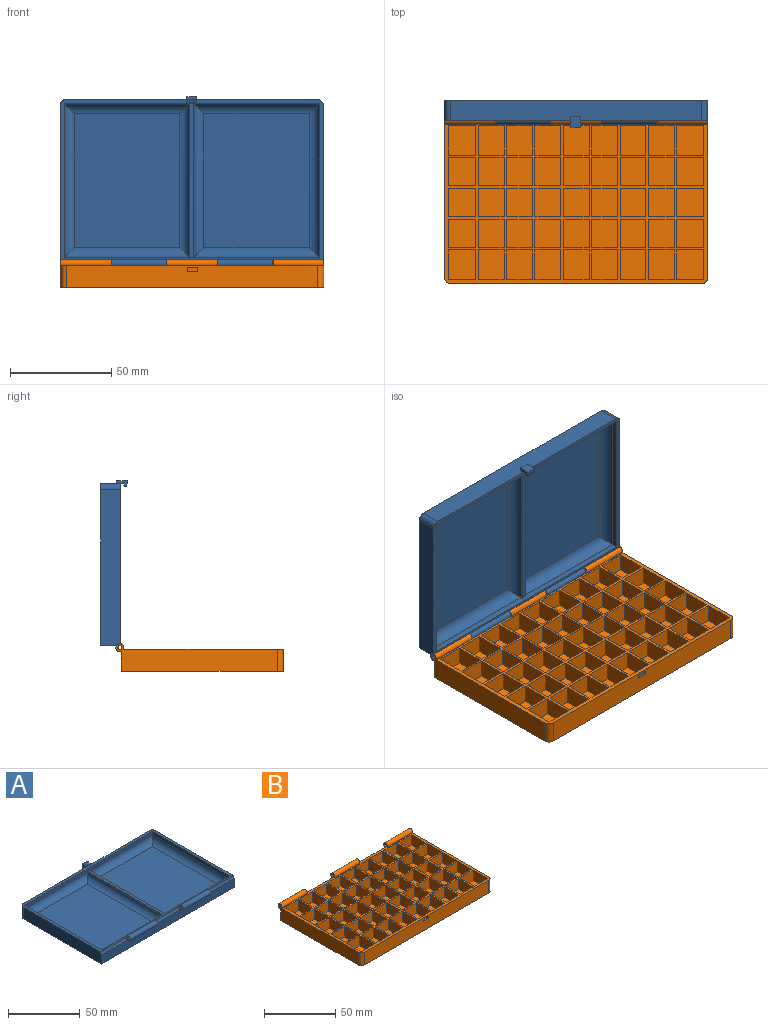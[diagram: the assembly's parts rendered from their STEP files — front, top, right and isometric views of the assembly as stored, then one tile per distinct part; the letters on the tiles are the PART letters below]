
ASSEMBLY  parts=2 mates=1
PART A: 45 faces, bbox 130x84.5x13.2 mm
  f0: cylinder r=2mm len=25mm, axis (1,0,0), area 62.8mm2, adj f2,f9,f20,f24
  f1: cylinder r=2mm len=25.25mm, axis (1,0,0), area 63.5mm2, adj f2,f3,f9,f21
  f2: plane 130x79.06mm, normal (0,0,1), area 697.5mm2, adj f0,f1,f3,f4,f5,f7,f8,f11
  f3: plane 77x10mm, normal (1,0,0), area 768.4mm2, adj f1,f2,f9,f10,f43
  f4: plane 126x3mm, normal (0,-1,0), area 376mm2, adj f2,f11,f12,f14,f15,f16,f36,f40
  f5: plane 126x3mm, normal (0,1,0), area 376mm2, adj f2,f11,f12,f14,f15,f16,f37,f41
  f6: plane 66x52mm, normal (0,0,1), area 3432mm2, adj f35,f36,f37,f38
  f7: plane 124x10mm, normal (0,1,0), area 1230.4mm2, adj f2,f10,f31,f33,f34,f43,f44
  f8: plane 77x10mm, normal (-1,0,0), area 768.4mm2, adj f2,f9,f10,f17,f44
  f9: plane 130x7.85mm, normal (0,-1,0), area 1020mm2, adj f0,f1,f3,f8,f10,f17,f18,f22
  f10: plane 130x80mm, normal (0,0,-1), area 10396.1mm2, adj f3,f7,f8,f9,f43,f44
  f11: plane 76x3mm, normal (1,0,0), area 228mm2, adj f2,f4,f5,f39
  f12: plane 76x3mm, normal (-1,0,0), area 228mm2, adj f2,f4,f5,f35
  f13: plane 66x52mm, normal (0,0,1), area 3432mm2, adj f39,f40,f41,f42
  f14: plane 76x2mm, normal (0,0,1), area 152mm2, adj f4,f5,f15,f16
  f15: plane 76x1mm, normal (1,0,0), area 76mm2, adj f4,f5,f14,f38
  f16: plane 76x1mm, normal (-1,0,0), area 76mm2, adj f4,f5,f14,f42
  f17: cylinder r=2mm len=25.25mm, axis (1,0,0), area 63.5mm2, adj f2,f8,f9,f25
  f18: cylinder r=2mm len=27.25mm, axis (1,0,0), area 273.9mm2, adj f2,f9,f20,f21
  f19: cylinder r=1mm len=27.25mm, axis (1,0,0), area 171.2mm2, adj f20,f21
  f20: plane 4x4mm, normal (-1,0,0), area 9.4mm2, adj f0,f18,f19
  f21: plane 4x4mm, normal (1,0,0), area 9.4mm2, adj f1,f18,f19
  f22: cylinder r=2mm len=27.25mm, axis (-1,0,0), area 273.9mm2, adj f2,f9,f24,f25
  f23: cylinder r=1mm len=27.25mm, axis (-1,0,0), area 171.2mm2, adj f24,f25
  f24: plane 4x4mm, normal (1,0,0), area 9.4mm2, adj f0,f22,f23
  f25: plane 4x4mm, normal (-1,0,0), area 9.4mm2, adj f17,f22,f23
  f26: plane 4.8x1.4mm, normal (0,-0.34,-0.94), area 7.1mm2, adj f27,f32,f33,f34
  f27: plane 4.8x1mm, normal (0,-1,0), area 4.8mm2, adj f26,f28,f33,f34
  f28: plane 4.8x1.4mm, normal (0,-0.34,0.94), area 7.1mm2, adj f27,f29,f33,f34
  f29: plane 4.8x1.5mm, normal (0,0,1), area 7.2mm2, adj f28,f30,f33,f34
  f30: plane 5.2x4.8mm, normal (0,1,0), area 25mm2, adj f29,f31,f33,f34
  f31: plane 4.8x1.5mm, normal (0,0,-1), area 7.2mm2, adj f7,f30,f33,f34
  f32: plane 4.8x1.2mm, normal (0,-1,0), area 5.8mm2, adj f2,f26,f33,f34
  f33: plane 5.2x2.9mm, normal (-1,0,0), area 9.9mm2, adj f7,f26,f27,f28,f29,f30,f31,f32
  f34: plane 5.2x2.9mm, normal (1,0,0), area 9.9mm2, adj f7,f26,f27,f28,f29,f30,f31,f32
  f35: cylinder r=5mm len=76mm, axis (0,-1,0), area 568.4mm2, adj f6,f12,f36,f37
  f36: cylinder r=5mm len=62mm, axis (1,0,0), area 458.4mm2, adj f4,f6,f35,f38
  f37: cylinder r=5mm len=62mm, axis (-1,0,0), area 458.4mm2, adj f5,f6,f35,f38
  f38: cylinder r=5mm len=76mm, axis (0,-1,0), area 568.4mm2, adj f6,f15,f36,f37
  f39: cylinder r=5mm len=76mm, axis (0,1,0), area 568.4mm2, adj f11,f13,f40,f41
  f40: cylinder r=5mm len=62mm, axis (1,0,0), area 458.4mm2, adj f4,f13,f39,f42
  f41: cylinder r=5mm len=62mm, axis (-1,0,0), area 458.4mm2, adj f5,f13,f39,f42
  f42: cylinder r=5mm len=76mm, axis (0,1,0), area 568.4mm2, adj f13,f16,f40,f41
  f43: cylinder r=3mm len=10mm, axis (0,0,-1), area 47.1mm2, adj f2,f3,f7,f10
  f44: cylinder r=3mm len=10mm, axis (0,0,1), area 47.1mm2, adj f2,f7,f8,f10
PART B: 248 faces, bbox 130x82.7x13.7 mm
  f0: plane 124x11mm, normal (0,-1,0), area 1354mm2, adj f1,f53,f241,f242,f244,f245,f246,f247
  f1: plane 130x80mm, normal (0,0,1), area 2021.2mm2, adj f0,f2,f3,f4,f5,f6,f7,f8
  f2: plane 130x11mm, normal (0,1,0), area 1342.7mm2, adj f1,f51,f52,f53,f231,f233,f234,f236
  f3: plane 13.4x9mm, normal (0,1,0), area 120.6mm2, adj f1,f26,f31,f91
  f4: plane 12.8x9mm, normal (0,1,0), area 115.2mm2, adj f1,f32,f92,f94
  f5: plane 12.8x9mm, normal (0,1,0), area 115.2mm2, adj f1,f33,f95,f97
  f6: plane 12.8x9mm, normal (0,1,0), area 115.2mm2, adj f1,f34,f98,f100
  f7: plane 12.8x9mm, normal (0,1,0), area 115.2mm2, adj f1,f35,f101,f103
  f8: plane 12.8x9mm, normal (0,1,0), area 115.2mm2, adj f1,f36,f104,f106
  f9: plane 12.8x9mm, normal (0,1,0), area 115.2mm2, adj f1,f37,f107,f109
  f10: plane 12.8x9mm, normal (0,1,0), area 115.2mm2, adj f1,f38,f110,f112
  f11: plane 14.6x9mm, normal (-1,0,0), area 131.4mm2, adj f1,f39,f54,f114
  f12: plane 14x9mm, normal (-1,0,0), area 126mm2, adj f1,f40,f115,f117
  f13: plane 14x9mm, normal (-1,0,0), area 126mm2, adj f1,f41,f118,f120
  f14: plane 14x9mm, normal (-1,0,0), area 126mm2, adj f1,f42,f121,f123
  f15: plane 13.4x9mm, normal (0,-1,0), area 120.6mm2, adj f1,f27,f57,f79
  f16: plane 12.8x9mm, normal (0,-1,0), area 115.2mm2, adj f1,f43,f126,f128
  f17: plane 12.8x9mm, normal (0,-1,0), area 115.2mm2, adj f1,f44,f129,f131
  f18: plane 12.8x9mm, normal (0,-1,0), area 115.2mm2, adj f1,f45,f132,f134
  f19: plane 12.8x9mm, normal (0,-1,0), area 115.2mm2, adj f1,f46,f135,f137
  f20: plane 12.8x9mm, normal (0,-1,0), area 115.2mm2, adj f1,f47,f138,f140
  f21: plane 12.8x9mm, normal (0,-1,0), area 115.2mm2, adj f1,f48,f141,f143
  f22: plane 12.8x9mm, normal (0,-1,0), area 115.2mm2, adj f1,f50,f78,f159
  f23: plane 14x9mm, normal (1,0,0), area 126mm2, adj f1,f28,f81,f83
  f24: plane 14x9mm, normal (1,0,0), area 126mm2, adj f1,f29,f84,f86
  f25: plane 14x9mm, normal (1,0,0), area 126mm2, adj f1,f30,f87,f89
  f26: plane 14.6x9mm, normal (1,0,0), area 131.4mm2, adj f1,f3,f31,f90
  f27: plane 14.6x13.4mm, normal (0,0,1), area 195.6mm2, adj f15,f57,f79,f80
  f28: plane 14x13.4mm, normal (0,0,1), area 187.6mm2, adj f23,f81,f82,f83
  f29: plane 14x13.4mm, normal (0,0,1), area 187.6mm2, adj f24,f84,f85,f86
  f30: plane 14x13.4mm, normal (0,0,1), area 187.6mm2, adj f25,f87,f88,f89
  f31: plane 14.6x13.4mm, normal (0,0,1), area 195.6mm2, adj f3,f26,f90,f91
  f32: plane 14.6x12.8mm, normal (0,0,1), area 186.9mm2, adj f4,f92,f93,f94
  f33: plane 14.6x12.8mm, normal (0,0,1), area 186.9mm2, adj f5,f95,f96,f97
  f34: plane 14.6x12.8mm, normal (0,0,1), area 186.9mm2, adj f6,f98,f99,f100
  f35: plane 14.6x12.8mm, normal (0,0,1), area 186.9mm2, adj f7,f101,f102,f103
  f36: plane 14.6x12.8mm, normal (0,0,1), area 186.9mm2, adj f8,f104,f105,f106
  f37: plane 14.6x12.8mm, normal (0,0,1), area 186.9mm2, adj f9,f107,f108,f109
  f38: plane 14.6x12.8mm, normal (0,0,1), area 186.9mm2, adj f10,f110,f111,f112
  f39: plane 14.6x13.4mm, normal (0,0,1), area 195.6mm2, adj f11,f54,f113,f114
  f40: plane 14x13.4mm, normal (0,0,1), area 187.6mm2, adj f12,f115,f116,f117
  f41: plane 14x13.4mm, normal (0,0,1), area 187.6mm2, adj f13,f118,f119,f120
  f42: plane 14x13.4mm, normal (0,0,1), area 187.6mm2, adj f14,f121,f122,f123
  f43: plane 14.6x12.8mm, normal (0,0,1), area 186.9mm2, adj f16,f126,f127,f128
  f44: plane 14.6x12.8mm, normal (0,0,1), area 186.9mm2, adj f17,f129,f130,f131
  f45: plane 14.6x12.8mm, normal (0,0,1), area 186.9mm2, adj f18,f132,f133,f134
  f46: plane 14.6x12.8mm, normal (0,0,1), area 186.9mm2, adj f19,f135,f136,f137
  f47: plane 14.6x12.8mm, normal (0,0,1), area 186.9mm2, adj f20,f138,f139,f140
  f48: plane 14.6x12.8mm, normal (0,0,1), area 186.9mm2, adj f21,f141,f142,f143
  f49: plane 14.6x13.4mm, normal (0,0,1), area 195.6mm2, adj f55,f56,f124,f125
  f50: plane 14.6x12.8mm, normal (0,0,1), area 186.9mm2, adj f22,f78,f152,f159
  f51: plane 79.71x13.71mm, normal (1,0,0), area 855.6mm2, adj f1,f2,f53,f231,f232,f246
  f52: plane 79.71x13.71mm, normal (-1,0,0), area 855.6mm2, adj f1,f2,f53,f234,f235,f247
  f53: plane 130x80mm, normal (0,0,-1), area 10396.1mm2, adj f0,f2,f51,f52,f246,f247
  f54: plane 13.4x9mm, normal (0,1,0), area 120.6mm2, adj f1,f11,f39,f113
  f55: plane 14.6x9mm, normal (-1,0,0), area 131.4mm2, adj f1,f49,f56,f124
  f56: plane 13.4x9mm, normal (0,-1,0), area 120.6mm2, adj f1,f49,f55,f125
  f57: plane 14.6x9mm, normal (1,0,0), area 131.4mm2, adj f1,f15,f27,f80
  f58: plane 12.8x9mm, normal (0,-1,0), area 115.2mm2, adj f1,f153,f154,f230
  f59: plane 12.8x9mm, normal (0,-1,0), area 115.2mm2, adj f1,f207,f208,f210
  f60: plane 12.8x9mm, normal (0,-1,0), area 115.2mm2, adj f1,f204,f205,f211
  f61: plane 12.8x9mm, normal (0,-1,0), area 115.2mm2, adj f1,f201,f202,f212
  f62: plane 12.8x9mm, normal (0,-1,0), area 115.2mm2, adj f1,f198,f199,f213
  f63: plane 14x9mm, normal (-1,0,0), area 126mm2, adj f1,f195,f196,f214
  f64: plane 12.8x9mm, normal (0,-1,0), area 115.2mm2, adj f1,f192,f193,f215
  f65: plane 14x9mm, normal (1,0,0), area 126mm2, adj f1,f145,f190,f216
  f66: plane 12.8x9mm, normal (0,1,0), area 115.2mm2, adj f1,f146,f188,f217
  f67: plane 12.8x9mm, normal (0,1,0), area 115.2mm2, adj f1,f147,f186,f218
  f68: plane 12.8x9mm, normal (0,1,0), area 115.2mm2, adj f1,f148,f184,f219
  f69: plane 14x9mm, normal (1,0,0), area 126mm2, adj f1,f149,f182,f220
  f70: plane 12.8x9mm, normal (0,1,0), area 115.2mm2, adj f1,f150,f180,f221
  f71: plane 14x9mm, normal (1,0,0), area 126mm2, adj f1,f151,f178,f222
  f72: plane 12.8x9mm, normal (0,-1,0), area 115.2mm2, adj f1,f175,f176,f223
  f73: plane 12.8x9mm, normal (0,-1,0), area 115.2mm2, adj f1,f172,f173,f224
  f74: plane 12.8x9mm, normal (0,-1,0), area 115.2mm2, adj f1,f169,f170,f225
  f75: plane 12.8x9mm, normal (0,-1,0), area 115.2mm2, adj f1,f166,f167,f226
  f76: plane 12.8x9mm, normal (0,-1,0), area 115.2mm2, adj f1,f163,f164,f227
  f77: plane 12.8x9mm, normal (0,-1,0), area 115.2mm2, adj f1,f160,f161,f228
  f78: plane 14.6x9mm, normal (1,0,0), area 131.4mm2, adj f1,f22,f50,f152
  f79: plane 14.6x9mm, normal (-1,0,0), area 131.4mm2, adj f1,f15,f27,f80
  f80: plane 13.4x9mm, normal (0,1,0), area 120.6mm2, adj f1,f27,f57,f79
  f81: plane 13.4x9mm, normal (0,-1,0), area 120.6mm2, adj f1,f23,f28,f82
  f82: plane 14x9mm, normal (-1,0,0), area 126mm2, adj f1,f28,f81,f83
  f83: plane 13.4x9mm, normal (0,1,0), area 120.6mm2, adj f1,f23,f28,f82
  f84: plane 13.4x9mm, normal (0,-1,0), area 120.6mm2, adj f1,f24,f29,f85
  f85: plane 14x9mm, normal (-1,0,0), area 126mm2, adj f1,f29,f84,f86
  f86: plane 13.4x9mm, normal (0,1,0), area 120.6mm2, adj f1,f24,f29,f85
  f87: plane 13.4x9mm, normal (0,-1,0), area 120.6mm2, adj f1,f25,f30,f88
  f88: plane 14x9mm, normal (-1,0,0), area 126mm2, adj f1,f30,f87,f89
  f89: plane 13.4x9mm, normal (0,1,0), area 120.6mm2, adj f1,f25,f30,f88
  f90: plane 13.4x9mm, normal (0,-1,0), area 120.6mm2, adj f1,f26,f31,f91
  f91: plane 14.6x9mm, normal (-1,0,0), area 131.4mm2, adj f1,f3,f31,f90
  f92: plane 14.6x9mm, normal (1,0,0), area 131.4mm2, adj f1,f4,f32,f93
  f93: plane 12.8x9mm, normal (0,-1,0), area 115.2mm2, adj f1,f32,f92,f94
  f94: plane 14.6x9mm, normal (-1,0,0), area 131.4mm2, adj f1,f4,f32,f93
  f95: plane 14.6x9mm, normal (1,0,0), area 131.4mm2, adj f1,f5,f33,f96
  f96: plane 12.8x9mm, normal (0,-1,0), area 115.2mm2, adj f1,f33,f95,f97
  f97: plane 14.6x9mm, normal (-1,0,0), area 131.4mm2, adj f1,f5,f33,f96
  f98: plane 14.6x9mm, normal (1,0,0), area 131.4mm2, adj f1,f6,f34,f99
  f99: plane 12.8x9mm, normal (0,-1,0), area 115.2mm2, adj f1,f34,f98,f100
  f100: plane 14.6x9mm, normal (-1,0,0), area 131.4mm2, adj f1,f6,f34,f99
  f101: plane 14.6x9mm, normal (1,0,0), area 131.4mm2, adj f1,f7,f35,f102
  f102: plane 12.8x9mm, normal (0,-1,0), area 115.2mm2, adj f1,f35,f101,f103
  f103: plane 14.6x9mm, normal (-1,0,0), area 131.4mm2, adj f1,f7,f35,f102
  f104: plane 14.6x9mm, normal (1,0,0), area 131.4mm2, adj f1,f8,f36,f105
  f105: plane 12.8x9mm, normal (0,-1,0), area 115.2mm2, adj f1,f36,f104,f106
  f106: plane 14.6x9mm, normal (-1,0,0), area 131.4mm2, adj f1,f8,f36,f105
  f107: plane 14.6x9mm, normal (1,0,0), area 131.4mm2, adj f1,f9,f37,f108
  f108: plane 12.8x9mm, normal (0,-1,0), area 115.2mm2, adj f1,f37,f107,f109
  f109: plane 14.6x9mm, normal (-1,0,0), area 131.4mm2, adj f1,f9,f37,f108
  f110: plane 14.6x9mm, normal (1,0,0), area 131.4mm2, adj f1,f10,f38,f111
  f111: plane 12.8x9mm, normal (0,-1,0), area 115.2mm2, adj f1,f38,f110,f112
  f112: plane 14.6x9mm, normal (-1,0,0), area 131.4mm2, adj f1,f10,f38,f111
  f113: plane 14.6x9mm, normal (1,0,0), area 131.4mm2, adj f1,f39,f54,f114
  f114: plane 13.4x9mm, normal (0,-1,0), area 120.6mm2, adj f1,f11,f39,f113
  f115: plane 13.4x9mm, normal (0,1,0), area 120.6mm2, adj f1,f12,f40,f116
  f116: plane 14x9mm, normal (1,0,0), area 126mm2, adj f1,f40,f115,f117
  f117: plane 13.4x9mm, normal (0,-1,0), area 120.6mm2, adj f1,f12,f40,f116
  f118: plane 13.4x9mm, normal (0,1,0), area 120.6mm2, adj f1,f13,f41,f119
  f119: plane 14x9mm, normal (1,0,0), area 126mm2, adj f1,f41,f118,f120
  f120: plane 13.4x9mm, normal (0,-1,0), area 120.6mm2, adj f1,f13,f41,f119
  f121: plane 13.4x9mm, normal (0,1,0), area 120.6mm2, adj f1,f14,f42,f122
  f122: plane 14x9mm, normal (1,0,0), area 126mm2, adj f1,f42,f121,f123
  f123: plane 13.4x9mm, normal (0,-1,0), area 120.6mm2, adj f1,f14,f42,f122
  f124: plane 13.4x9mm, normal (0,1,0), area 120.6mm2, adj f1,f49,f55,f125
  f125: plane 14.6x9mm, normal (1,0,0), area 131.4mm2, adj f1,f49,f56,f124
  f126: plane 14.6x9mm, normal (-1,0,0), area 131.4mm2, adj f1,f16,f43,f127
  f127: plane 12.8x9mm, normal (0,1,0), area 115.2mm2, adj f1,f43,f126,f128
  f128: plane 14.6x9mm, normal (1,0,0), area 131.4mm2, adj f1,f16,f43,f127
  f129: plane 14.6x9mm, normal (-1,0,0), area 131.4mm2, adj f1,f17,f44,f130
  f130: plane 12.8x9mm, normal (0,1,0), area 115.2mm2, adj f1,f44,f129,f131
  f131: plane 14.6x9mm, normal (1,0,0), area 131.4mm2, adj f1,f17,f44,f130
  f132: plane 14.6x9mm, normal (-1,0,0), area 131.4mm2, adj f1,f18,f45,f133
  f133: plane 12.8x9mm, normal (0,1,0), area 115.2mm2, adj f1,f45,f132,f134
  f134: plane 14.6x9mm, normal (1,0,0), area 131.4mm2, adj f1,f18,f45,f133
  f135: plane 14.6x9mm, normal (-1,0,0), area 131.4mm2, adj f1,f19,f46,f136
  f136: plane 12.8x9mm, normal (0,1,0), area 115.2mm2, adj f1,f46,f135,f137
  f137: plane 14.6x9mm, normal (1,0,0), area 131.4mm2, adj f1,f19,f46,f136
  f138: plane 14.6x9mm, normal (-1,0,0), area 131.4mm2, adj f1,f20,f47,f139
  f139: plane 12.8x9mm, normal (0,1,0), area 115.2mm2, adj f1,f47,f138,f140
  f140: plane 14.6x9mm, normal (1,0,0), area 131.4mm2, adj f1,f20,f47,f139
  f141: plane 14.6x9mm, normal (-1,0,0), area 131.4mm2, adj f1,f21,f48,f142
  f142: plane 12.8x9mm, normal (0,1,0), area 115.2mm2, adj f1,f48,f141,f143
  f143: plane 14.6x9mm, normal (1,0,0), area 131.4mm2, adj f1,f21,f48,f142
  f144: plane 12.8x9mm, normal (0,-1,0), area 115.2mm2, adj f1,f156,f157,f229
  f145: plane 12.8x9mm, normal (0,1,0), area 115.2mm2, adj f1,f65,f191,f216
  f146: plane 14x9mm, normal (-1,0,0), area 126mm2, adj f1,f66,f189,f217
  f147: plane 14x9mm, normal (-1,0,0), area 126mm2, adj f1,f67,f187,f218
  f148: plane 14x9mm, normal (-1,0,0), area 126mm2, adj f1,f68,f185,f219
  f149: plane 12.8x9mm, normal (0,1,0), area 115.2mm2, adj f1,f69,f183,f220
  f150: plane 14x9mm, normal (-1,0,0), area 126mm2, adj f1,f70,f181,f221
  f151: plane 12.8x9mm, normal (0,1,0), area 115.2mm2, adj f1,f71,f179,f222
  f152: plane 12.8x9mm, normal (0,1,0), area 115.2mm2, adj f1,f50,f78,f159
  f153: plane 14x9mm, normal (-1,0,0), area 126mm2, adj f1,f58,f155,f230
  f154: plane 14x9mm, normal (1,0,0), area 126mm2, adj f1,f58,f155,f230
  f155: plane 12.8x9mm, normal (0,1,0), area 115.2mm2, adj f1,f153,f154,f230
  f156: plane 14x9mm, normal (-1,0,0), area 126mm2, adj f1,f144,f158,f229
  f157: plane 14x9mm, normal (1,0,0), area 126mm2, adj f1,f144,f158,f229
  f158: plane 12.8x9mm, normal (0,1,0), area 115.2mm2, adj f1,f156,f157,f229
  f159: plane 14.6x9mm, normal (-1,0,0), area 131.4mm2, adj f1,f22,f50,f152
  f160: plane 14x9mm, normal (-1,0,0), area 126mm2, adj f1,f77,f162,f228
  f161: plane 14x9mm, normal (1,0,0), area 126mm2, adj f1,f77,f162,f228
  f162: plane 12.8x9mm, normal (0,1,0), area 115.2mm2, adj f1,f160,f161,f228
  f163: plane 14x9mm, normal (-1,0,0), area 126mm2, adj f1,f76,f165,f227
  f164: plane 14x9mm, normal (1,0,0), area 126mm2, adj f1,f76,f165,f227
  f165: plane 12.8x9mm, normal (0,1,0), area 115.2mm2, adj f1,f163,f164,f227
  f166: plane 14x9mm, normal (-1,0,0), area 126mm2, adj f1,f75,f168,f226
  f167: plane 14x9mm, normal (1,0,0), area 126mm2, adj f1,f75,f168,f226
  f168: plane 12.8x9mm, normal (0,1,0), area 115.2mm2, adj f1,f166,f167,f226
  f169: plane 14x9mm, normal (-1,0,0), area 126mm2, adj f1,f74,f171,f225
  f170: plane 14x9mm, normal (1,0,0), area 126mm2, adj f1,f74,f171,f225
  f171: plane 12.8x9mm, normal (0,1,0), area 115.2mm2, adj f1,f169,f170,f225
  f172: plane 14x9mm, normal (-1,0,0), area 126mm2, adj f1,f73,f174,f224
  f173: plane 14x9mm, normal (1,0,0), area 126mm2, adj f1,f73,f174,f224
  f174: plane 12.8x9mm, normal (0,1,0), area 115.2mm2, adj f1,f172,f173,f224
  f175: plane 14x9mm, normal (-1,0,0), area 126mm2, adj f1,f72,f177,f223
  f176: plane 14x9mm, normal (1,0,0), area 126mm2, adj f1,f72,f177,f223
  f177: plane 12.8x9mm, normal (0,1,0), area 115.2mm2, adj f1,f175,f176,f223
  f178: plane 12.8x9mm, normal (0,-1,0), area 115.2mm2, adj f1,f71,f179,f222
  f179: plane 14x9mm, normal (-1,0,0), area 126mm2, adj f1,f151,f178,f222
  f180: plane 14x9mm, normal (1,0,0), area 126mm2, adj f1,f70,f181,f221
  f181: plane 12.8x9mm, normal (0,-1,0), area 115.2mm2, adj f1,f150,f180,f221
  f182: plane 12.8x9mm, normal (0,-1,0), area 115.2mm2, adj f1,f69,f183,f220
  f183: plane 14x9mm, normal (-1,0,0), area 126mm2, adj f1,f149,f182,f220
  f184: plane 14x9mm, normal (1,0,0), area 126mm2, adj f1,f68,f185,f219
  f185: plane 12.8x9mm, normal (0,-1,0), area 115.2mm2, adj f1,f148,f184,f219
  f186: plane 14x9mm, normal (1,0,0), area 126mm2, adj f1,f67,f187,f218
  f187: plane 12.8x9mm, normal (0,-1,0), area 115.2mm2, adj f1,f147,f186,f218
  f188: plane 14x9mm, normal (1,0,0), area 126mm2, adj f1,f66,f189,f217
  f189: plane 12.8x9mm, normal (0,-1,0), area 115.2mm2, adj f1,f146,f188,f217
  f190: plane 12.8x9mm, normal (0,-1,0), area 115.2mm2, adj f1,f65,f191,f216
  f191: plane 14x9mm, normal (-1,0,0), area 126mm2, adj f1,f145,f190,f216
  f192: plane 14x9mm, normal (-1,0,0), area 126mm2, adj f1,f64,f194,f215
  f193: plane 14x9mm, normal (1,0,0), area 126mm2, adj f1,f64,f194,f215
  f194: plane 12.8x9mm, normal (0,1,0), area 115.2mm2, adj f1,f192,f193,f215
  f195: plane 12.8x9mm, normal (0,1,0), area 115.2mm2, adj f1,f63,f197,f214
  f196: plane 12.8x9mm, normal (0,-1,0), area 115.2mm2, adj f1,f63,f197,f214
  f197: plane 14x9mm, normal (1,0,0), area 126mm2, adj f1,f195,f196,f214
  f198: plane 14x9mm, normal (-1,0,0), area 126mm2, adj f1,f62,f200,f213
  f199: plane 14x9mm, normal (1,0,0), area 126mm2, adj f1,f62,f200,f213
  f200: plane 12.8x9mm, normal (0,1,0), area 115.2mm2, adj f1,f198,f199,f213
  f201: plane 14x9mm, normal (-1,0,0), area 126mm2, adj f1,f61,f203,f212
  f202: plane 14x9mm, normal (1,0,0), area 126mm2, adj f1,f61,f203,f212
  f203: plane 12.8x9mm, normal (0,1,0), area 115.2mm2, adj f1,f201,f202,f212
  f204: plane 14x9mm, normal (-1,0,0), area 126mm2, adj f1,f60,f206,f211
  f205: plane 14x9mm, normal (1,0,0), area 126mm2, adj f1,f60,f206,f211
  f206: plane 12.8x9mm, normal (0,1,0), area 115.2mm2, adj f1,f204,f205,f211
  f207: plane 14x9mm, normal (-1,0,0), area 126mm2, adj f1,f59,f209,f210
  f208: plane 14x9mm, normal (1,0,0), area 126mm2, adj f1,f59,f209,f210
  f209: plane 12.8x9mm, normal (0,1,0), area 115.2mm2, adj f1,f207,f208,f210
  f210: plane 14x12.8mm, normal (0,0,1), area 179.2mm2, adj f59,f207,f208,f209
  f211: plane 14x12.8mm, normal (0,0,1), area 179.2mm2, adj f60,f204,f205,f206
  f212: plane 14x12.8mm, normal (0,0,1), area 179.2mm2, adj f61,f201,f202,f203
  f213: plane 14x12.8mm, normal (0,0,1), area 179.2mm2, adj f62,f198,f199,f200
  f214: plane 14x12.8mm, normal (0,0,1), area 179.2mm2, adj f63,f195,f196,f197
  f215: plane 14x12.8mm, normal (0,0,1), area 179.2mm2, adj f64,f192,f193,f194
  f216: plane 14x12.8mm, normal (0,0,1), area 179.2mm2, adj f65,f145,f190,f191
  f217: plane 14x12.8mm, normal (0,0,1), area 179.2mm2, adj f66,f146,f188,f189
  f218: plane 14x12.8mm, normal (0,0,1), area 179.2mm2, adj f67,f147,f186,f187
  f219: plane 14x12.8mm, normal (0,0,1), area 179.2mm2, adj f68,f148,f184,f185
  f220: plane 14x12.8mm, normal (0,0,1), area 179.2mm2, adj f69,f149,f182,f183
  f221: plane 14x12.8mm, normal (0,0,1), area 179.2mm2, adj f70,f150,f180,f181
  f222: plane 14x12.8mm, normal (0,0,1), area 179.2mm2, adj f71,f151,f178,f179
  f223: plane 14x12.8mm, normal (0,0,1), area 179.2mm2, adj f72,f175,f176,f177
  f224: plane 14x12.8mm, normal (0,0,1), area 179.2mm2, adj f73,f172,f173,f174
  f225: plane 14x12.8mm, normal (0,0,1), area 179.2mm2, adj f74,f169,f170,f171
  f226: plane 14x12.8mm, normal (0,0,1), area 179.2mm2, adj f75,f166,f167,f168
  f227: plane 14x12.8mm, normal (0,0,1), area 179.2mm2, adj f76,f163,f164,f165
  f228: plane 14x12.8mm, normal (0,0,1), area 179.2mm2, adj f77,f160,f161,f162
  f229: plane 14x12.8mm, normal (0,0,1), area 179.2mm2, adj f144,f156,f157,f158
  f230: plane 14x12.8mm, normal (0,0,1), area 179.2mm2, adj f58,f153,f154,f155
  f231: cylinder r=2mm len=25mm, axis (1,0,0), area 271.8mm2, adj f1,f2,f51,f233
  f232: cylinder r=1mm len=25mm, axis (1,0,0), area 157.1mm2, adj f51,f233
  f233: plane 4x4mm, normal (-1,0,0), area 8.6mm2, adj f1,f2,f231,f232
  f234: cylinder r=2mm len=25mm, axis (-1,0,0), area 271.8mm2, adj f1,f2,f52,f236
  f235: cylinder r=1mm len=25mm, axis (-1,0,0), area 157.1mm2, adj f52,f236
  f236: plane 4x4mm, normal (1,0,0), area 8.6mm2, adj f1,f2,f234,f235
  f237: cylinder r=1mm len=25mm, axis (-1,0,0), area 157.1mm2, adj f239,f240
  f238: cylinder r=2mm len=25mm, axis (-1,0,0), area 271.8mm2, adj f1,f2,f239,f240
  f239: plane 4x4mm, normal (1,0,0), area 8.6mm2, adj f1,f2,f237,f238
  f240: plane 4x4mm, normal (-1,0,0), area 8.6mm2, adj f1,f2,f237,f238
  f241: plane 5x1mm, normal (0,0,-1), area 5mm2, adj f0,f243,f244,f245
  f242: plane 5x1mm, normal (0,0,1), area 5mm2, adj f0,f243,f244,f245
  f243: plane 5x2mm, normal (0,-1,0), area 10mm2, adj f241,f242,f244,f245
  f244: plane 2x1mm, normal (-1,0,0), area 2mm2, adj f0,f241,f242,f243
  f245: plane 2x1mm, normal (1,0,0), area 2mm2, adj f0,f241,f242,f243
  f246: cylinder r=3mm len=11mm, axis (0,0,1), area 51.8mm2, adj f0,f1,f51,f53
  f247: cylinder r=3mm len=11mm, axis (0,0,-1), area 51.8mm2, adj f0,f1,f52,f53
PLACE A rot(axis=(1,0,0),90deg) t=(44,106.93,21.18)mm
PLACE B t=(44.25,16.65,8.46)mm
MATE revolute B.f231 <-> A.f22  axis (1,0,0) through (-60.75,97.36,20.17)mm
